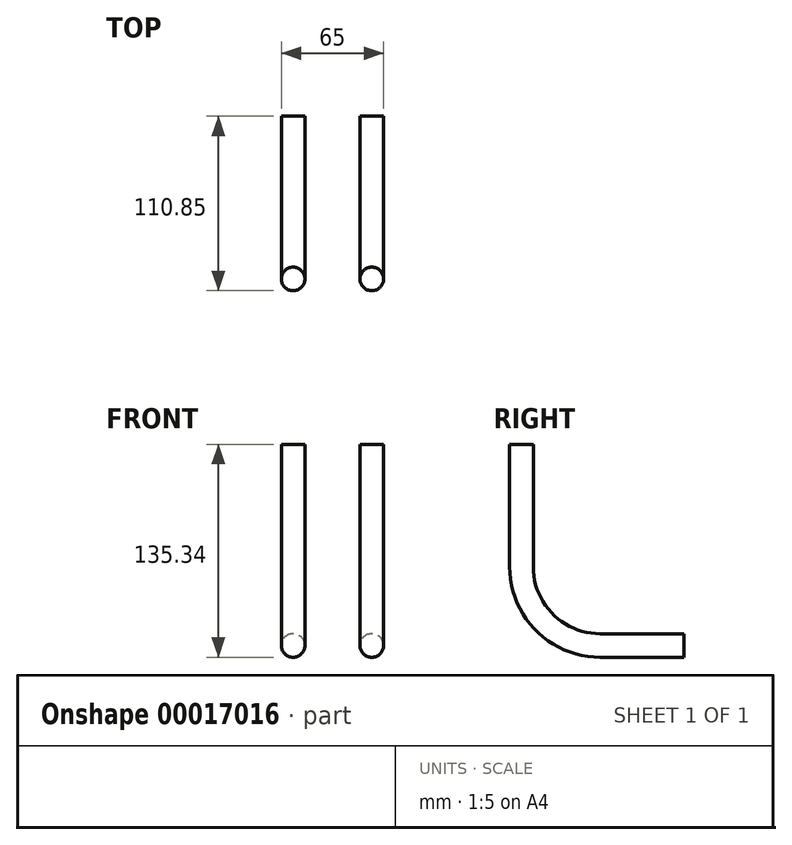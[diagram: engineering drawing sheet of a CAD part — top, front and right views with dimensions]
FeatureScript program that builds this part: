
annotation { "Feature Type Name" : "Feature", "Feature Type Description" : "" }
export const myFeature = defineFeature(function(context is Context, id is Id, definition is map)
    precondition{}
    {
        {
            var Q0;
            Q0=qCreatedBy(makeId("Right.planeOp"),FACE);
            cPlane(context, id + "F0", {"entities" : qUnion([Q0]), "cplaneType" : CPlaneType.OFFSET, "offset" : 50 * mm, "width" : 150 * mm, "height" : 150 * mm});
        }
        {
            var Q0;
            Q0=qCreatedBy(makeId("Right.planeOp"),FACE);
            var sketch = newSketch(context, id + "F1", { "sketchPlane" : qUnion([Q0])});
            skLineSegment(sketch, "E0", {"start": v(0, 127.84) * mm, "end": v(0, 50) * mm});
            skLineSegment(sketch, "E1", {"start": v(50, 0) * mm, "end": v(103.35, 0) * mm});
            skPoint(sketch, "E2.visualSharp", {"position": v(0, 0) * mm});
            skArc(sketch, "E2.filletArc", {"start": v(0, 50) * mm, "mid": v(14.64, 14.64) * mm, "end": v(50, 0) * mm});
            skSolve(sketch);
        }
        {
            var Q0;
            Q0=qCreatedBy(id+"F0.planeOp",FACE);
            var sketch = newSketch(context, id + "F2", { "sketchPlane" : qUnion([Q0])});
            skLineSegment(sketch, "E3.0", {"start": v(0, 127.84) * mm, "end": v(0, 50) * mm});
            skArc(sketch, "E3.1", {"start": v(0, 50) * mm, "mid": v(14.64, 14.64) * mm, "end": v(50, 0) * mm});
            skLineSegment(sketch, "E3.2", {"start": v(50, 0) * mm, "end": v(103.35, 0) * mm});
            skSolve(sketch);
        }
        {
            var Q0;
            Q0=sQuery(id+"F1.wireOp",EDGE,"E0");
            var Q1;
            Q1=sQuery(id+"F1.wireOp",VERTEX,"E0.start");
            cPlane(context, id + "F3", {"entities" : qUnion([Q0, Q1]), "cplaneType" : CPlaneType.LINE_POINT, "offset" : 150 * mm, "width" : 150 * mm, "height" : 150 * mm});
        }
        {
            var Q0;
            Q0=qCreatedBy(id+"F3.planeOp",FACE);
            cPlane(context, id + "F4", {"entities" : qUnion([Q0]), "cplaneType" : CPlaneType.OFFSET, "offset" : 30 * mm, "width" : 150 * mm, "height" : 150 * mm});
        }
        {
            var Q0;
            Q0=qCreatedBy(id+"F3.planeOp",FACE);
            var sketch = newSketch(context, id + "F5", { "sketchPlane" : qUnion([Q0])});
            skCircle(sketch, "E4", {"center": v(0, 0) * mm, "radius": 7.5 * mm});
            skSolve(sketch);
        }
        {
            var Q0;
            Q0=qCreatedBy(id+"F4.planeOp",FACE);
            var sketch = newSketch(context, id + "F6", { "sketchPlane" : qUnion([Q0])});
            skCircle(sketch, "E5", {"center": v(50, 0) * mm, "radius": 7.5 * mm});
            skSolve(sketch);
        }
        {
            var Q0;
            Q0=makeQuery(id+"F5.imprint","IMPRINT",FACE,{"disambiguationData":[TD([[makeQuery(id+"F5.imprint","IMPRINT",EDGE,{"derivedFrom":sQuery(id+"F5.wireOp",EDGE,"E4")}),1.0]])]});
            var Q1;
            Q1=sQuery(id+"F1.wireOp",EDGE,"E0");
            var Q2;
            Q2=sQuery(id+"F1.wireOp",EDGE,"E2.filletArc");
            var Q3;
            Q3=sQuery(id+"F1.wireOp",EDGE,"E1");
            sweep(context, id + "F7", {"profiles" : qUnion([Q0]), "path" : qUnion([Q1, Q2, Q3])});
        }
        {
            var Q0;
            Q0=makeQuery(id+"F6.imprint","IMPRINT",FACE,{"disambiguationData":[TD([[makeQuery(id+"F6.imprint","IMPRINT",EDGE,{"derivedFrom":sQuery(id+"F6.wireOp",EDGE,"E5")}),1.0]])]});
            var Q1;
            Q1=sQuery(id+"F2.wireOp",EDGE,"E3.0");
            var Q2;
            Q2=sQuery(id+"F2.wireOp",EDGE,"E3.1");
            var Q3;
            Q3=sQuery(id+"F2.wireOp",EDGE,"E3.2");
            sweep(context, id + "F8", {"profiles" : qUnion([Q0]), "path" : qUnion([Q1, Q2, Q3])});
        }
    });
